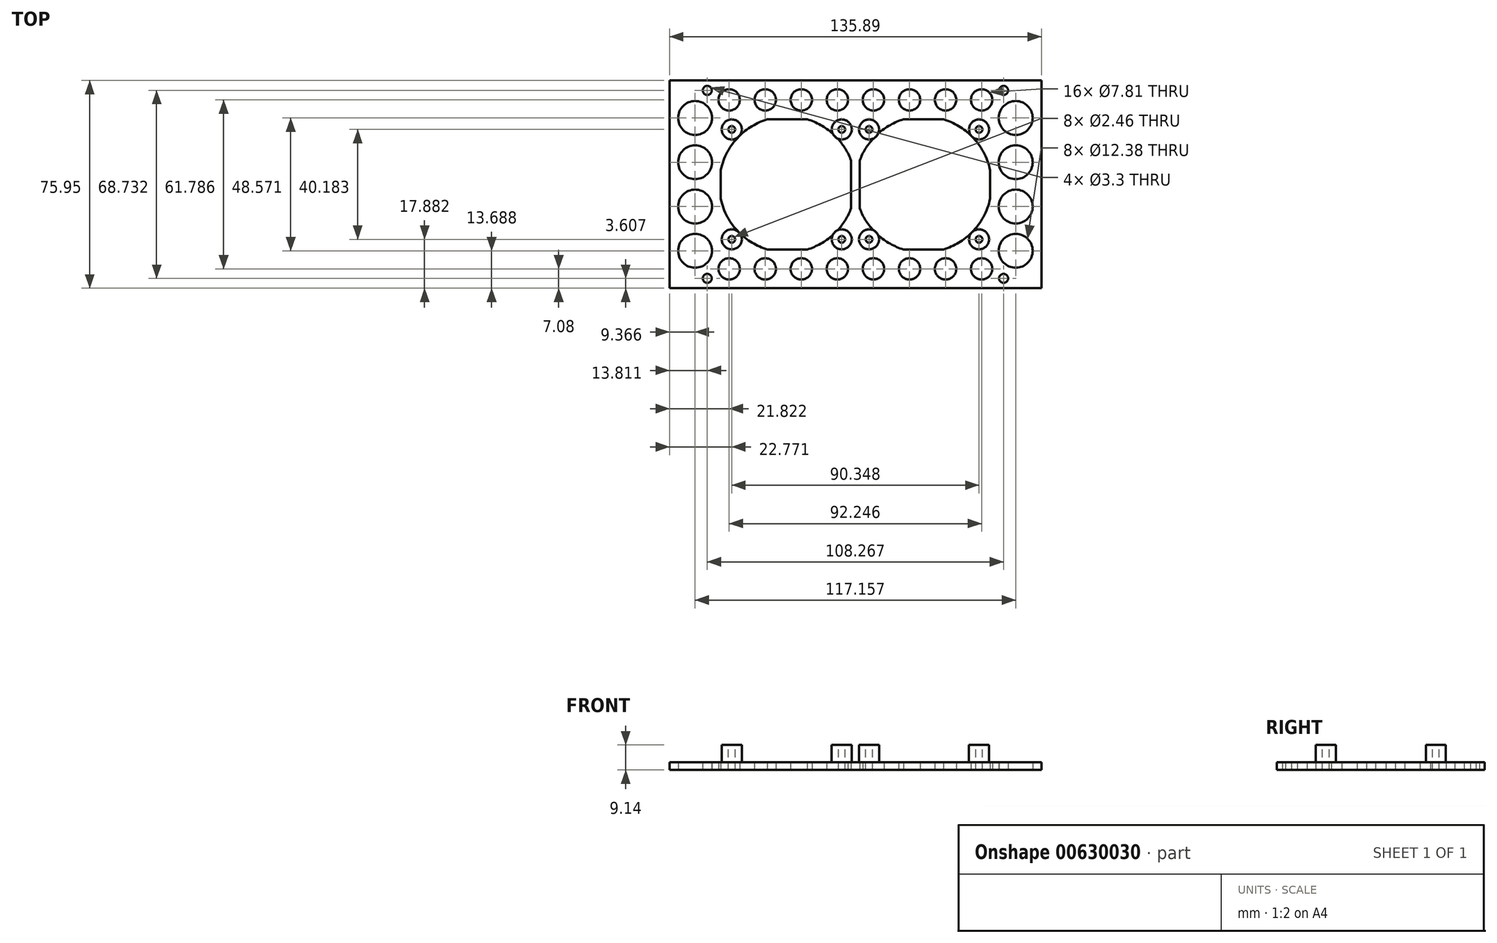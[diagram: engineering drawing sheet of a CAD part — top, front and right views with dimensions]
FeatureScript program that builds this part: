
annotation { "Feature Type Name" : "Feature", "Feature Type Description" : "" }
export const myFeature = defineFeature(function(context is Context, id is Id, definition is map)
    precondition{}
    {
        {
            var Q0;
            Q0=qCreatedBy(makeId("Top.planeOp"),FACE);
            var sketch = newSketch(context, id + "F0", { "sketchPlane" : qUnion([Q0])});
            skLineSegment(sketch, "E0.bottom", {"start": v(0, 0) * mm, "end": v(135.9, 0) * mm});
            skLineSegment(sketch, "E0.top", {"start": v(0, 75.95) * mm, "end": v(135.9, 75.95) * mm});
            skLineSegment(sketch, "E0.left", {"start": v(0, 0) * mm, "end": v(0, 75.95) * mm});
            skLineSegment(sketch, "E0.right", {"start": v(135.9, 0) * mm, "end": v(135.9, 75.95) * mm});
            skLineSegment(sketch, "E1", {"start": v(67.95, 0) * mm, "end": v(67.95, 37.97) * mm, "construction": true});
            skLineSegment(sketch, "E2", {"start": v(0, 37.97) * mm, "end": v(176.32, 37.97) * mm, "construction": true});
            skCircle(sketch, "E3", {"center": v(13.81, 72.34) * mm, "radius": 1.65 * mm});
            skCircle(sketch, "E4.MirrorC", {"center": v(122.08, 72.34) * mm, "radius": 1.65 * mm});
            skCircle(sketch, "E5.MirrorC", {"center": v(13.81, 3.6) * mm, "radius": 1.65 * mm});
            skCircle(sketch, "E6.MirrorC", {"center": v(122.08, 3.6) * mm, "radius": 1.65 * mm});
            skLineSegment(sketch, "E7.bottom", {"start": v(35.8, 61.79) * mm, "end": v(50.3, 61.79) * mm});
            skLineSegment(sketch, "E7.top", {"start": v(35.8, 14.16) * mm, "end": v(50.3, 14.16) * mm});
            skLineSegment(sketch, "E7.left", {"start": v(18.73, 43.28) * mm, "end": v(18.73, 32.67) * mm});
            skLineSegment(sketch, "E7.right", {"start": v(117.16, 43.28) * mm, "end": v(117.16, 32.67) * mm});
            skLineSegment(sketch, "E8", {"start": v(18.73, 61.79) * mm, "end": v(117.16, 14.16) * mm, "construction": true});
            skArc(sketch, "E9", {"start": v(66.36, 46.72) * mm, "mid": v(60.09, 56.12) * mm, "end": v(50.3, 61.79) * mm});
            skArc(sketch, "E10.MirrorC", {"start": v(69.53, 46.72) * mm, "mid": v(75.8, 56.12) * mm, "end": v(85.59, 61.79) * mm});
            skLineSegment(sketch, "E11", {"start": v(66.36, 29.23) * mm, "end": v(66.36, 46.72) * mm});
            skLineSegment(sketch, "E12.MirrorCS", {"start": v(69.53, 29.23) * mm, "end": v(69.53, 46.72) * mm});
            skPoint(sketch, "E13.orphan", {"position": v(66.36, 52.96) * mm});
            skPoint(sketch, "E14.orphan", {"position": v(69.53, 52.96) * mm});
            skPoint(sketch, "E15.orphan", {"position": v(66.36, 20.8) * mm});
            skPoint(sketch, "E16.orphan", {"position": v(69.53, 20.8) * mm});
            skLineSegment(sketch, "E17.trimOffspring", {"start": v(85.59, 14.16) * mm, "end": v(100.09, 14.16) * mm});
            skLineSegment(sketch, "E18.trimOffspring", {"start": v(85.59, 61.79) * mm, "end": v(100.09, 61.79) * mm});
            skArc(sketch, "E19.trimOffspring", {"start": v(85.59, 14.16) * mm, "mid": v(75.8, 19.82) * mm, "end": v(69.53, 29.23) * mm});
            skArc(sketch, "E20.trimOffspring", {"start": v(117.16, 32.67) * mm, "mid": v(111.14, 21.1) * mm, "end": v(100.09, 14.16) * mm});
            skArc(sketch, "E21.trimOffspring", {"start": v(100.09, 61.79) * mm, "mid": v(111.14, 54.85) * mm, "end": v(117.16, 43.28) * mm});
            skArc(sketch, "E22.trimOffspring", {"start": v(35.8, 61.79) * mm, "mid": v(24.75, 54.85) * mm, "end": v(18.73, 43.28) * mm});
            skArc(sketch, "E23.trimOffspring", {"start": v(18.73, 32.67) * mm, "mid": v(24.75, 21.1) * mm, "end": v(35.8, 14.16) * mm});
            skArc(sketch, "E24.trimOffspring", {"start": v(50.3, 14.16) * mm, "mid": v(60.09, 19.82) * mm, "end": v(66.36, 29.23) * mm});
            skSolve(sketch);
        }
        {
            var Q0;
            Q0 = qSketchRegion(id + "F0", true);
            extrude(context, id + "F1", {"entities" : qUnion([Q0]), "depth" : 2.8 * mm, "offsetDistance" : 25.4 * mm});
        }
        {
            var Q0;
            Q0=makeQuery(id+"F1.opExtrude","CAP_FACE",FACE,{"disambiguationData":[OSD([sQuery(id+"F0.wireOp",EDGE,"E0.bottom"),sQuery(id+"F0.wireOp",EDGE,"E0.top"),sQuery(id+"F0.wireOp",EDGE,"E0.left"),sQuery(id+"F0.wireOp",EDGE,"E0.right"),sQuery(id+"F0.wireOp",EDGE,"E3"),sQuery(id+"F0.wireOp",EDGE,"E4.MirrorC"),sQuery(id+"F0.wireOp",EDGE,"E5.MirrorC"),sQuery(id+"F0.wireOp",EDGE,"E6.MirrorC"),sQuery(id+"F0.wireOp",EDGE,"E7.bottom"),sQuery(id+"F0.wireOp",EDGE,"E7.top"),sQuery(id+"F0.wireOp",EDGE,"E7.left"),sQuery(id+"F0.wireOp",EDGE,"E7.right"),sQuery(id+"F0.wireOp",EDGE,"E9"),sQuery(id+"F0.wireOp",EDGE,"E10.MirrorC"),sQuery(id+"F0.wireOp",EDGE,"E11"),sQuery(id+"F0.wireOp",EDGE,"E12.MirrorCS"),sQuery(id+"F0.wireOp",EDGE,"E17.trimOffspring"),sQuery(id+"F0.wireOp",EDGE,"E18.trimOffspring"),sQuery(id+"F0.wireOp",EDGE,"E19.trimOffspring"),sQuery(id+"F0.wireOp",EDGE,"E20.trimOffspring"),sQuery(id+"F0.wireOp",EDGE,"E21.trimOffspring"),sQuery(id+"F0.wireOp",EDGE,"E22.trimOffspring"),sQuery(id+"F0.wireOp",EDGE,"E23.trimOffspring"),sQuery(id+"F0.wireOp",EDGE,"E24.trimOffspring")])],"isStart":false});
            var sketch = newSketch(context, id + "F2", { "sketchPlane" : qUnion([Q0])});
            skSolve(sketch);
        }
        {
            var Q0;
            Q0=makeQuery(id+"F2.imprint","IMPRINT",FACE,{"disambiguationData":[TD([[makeQuery(id+"F2.imprint","IMPRINT",EDGE,{"derivedFrom":makeQuery(id+"F1.opExtrude","CAP_EDGE",EDGE,{"disambiguationData":[OSD([sQuery(id+"F0.wireOp",EDGE,"E0.bottom")])],"isStart":false})}),1.0]])]});
            var sketch = newSketch(context, id + "F3", { "sketchPlane" : qUnion([Q0])});
            skLineSegment(sketch, "E25", {"start": v(66.36, 37.97) * mm, "end": v(69.53, 37.97) * mm, "construction": true});
            skLineSegment(sketch, "E26", {"start": v(67.94, 78.79) * mm, "end": v(67.94, 37.97) * mm, "construction": true});
            skCircle(sketch, "E27", {"center": v(22.77, 58.06) * mm, "radius": 1.23 * mm});
            skCircle(sketch, "E28", {"center": v(62.95, 58.06) * mm, "radius": 1.23 * mm});
            skCircle(sketch, "E29.MirrorC", {"center": v(72.94, 58.06) * mm, "radius": 1.23 * mm});
            skCircle(sketch, "E30.MirrorC", {"center": v(113.12, 58.06) * mm, "radius": 1.23 * mm});
            skCircle(sketch, "E31.MirrorC", {"center": v(113.12, 17.88) * mm, "radius": 1.23 * mm});
            skCircle(sketch, "E32.MirrorC", {"center": v(72.94, 17.88) * mm, "radius": 1.23 * mm});
            skCircle(sketch, "E33.MirrorC", {"center": v(62.95, 17.88) * mm, "radius": 1.23 * mm});
            skCircle(sketch, "E34.MirrorC", {"center": v(22.77, 17.88) * mm, "radius": 1.23 * mm});
            skSolve(sketch);
        }
        {
            var Q0;
            Q0 = qSketchRegion(id + "F3", true);
            extrude(context, id + "F4", {"entities" : qUnion([Q0]), "operationType" : NewBodyOperationType.REMOVE, "endBound" : BoundingType.THROUGH_ALL, "oppositeDirection" : true, "depth" : 25.4 * mm, "offsetDistance" : 25.4 * mm});
        }
        {
            var Q0;
            Q0=makeQuery(id+"F2.imprint","IMPRINT",FACE,{"disambiguationData":[TD([[makeQuery(id+"F2.imprint","IMPRINT",EDGE,{"derivedFrom":makeQuery(id+"F1.opExtrude","CAP_EDGE",EDGE,{"disambiguationData":[OSD([sQuery(id+"F0.wireOp",EDGE,"E0.bottom")])],"isStart":false})}),1.0]])]});
            var sketch = newSketch(context, id + "F5", { "sketchPlane" : qUnion([Q0])});
            skCircle(sketch, "E35.0", {"center": v(22.77, 58.06) * mm, "radius": 1.23 * mm});
            skCircle(sketch, "E35.1", {"center": v(22.77, 17.88) * mm, "radius": 1.23 * mm});
            skCircle(sketch, "E35.2", {"center": v(62.95, 17.88) * mm, "radius": 1.23 * mm});
            skCircle(sketch, "E35.3", {"center": v(62.95, 58.06) * mm, "radius": 1.23 * mm});
            skCircle(sketch, "E35.4", {"center": v(72.94, 58.06) * mm, "radius": 1.23 * mm});
            skCircle(sketch, "E35.5", {"center": v(72.94, 17.88) * mm, "radius": 1.23 * mm});
            skCircle(sketch, "E35.6", {"center": v(113.12, 58.06) * mm, "radius": 1.23 * mm});
            skCircle(sketch, "E35.7", {"center": v(113.12, 17.88) * mm, "radius": 1.23 * mm});
            skCircle(sketch, "E36", {"center": v(22.77, 58.06) * mm, "radius": 3.66 * mm});
            skCircle(sketch, "E37", {"center": v(62.95, 58.06) * mm, "radius": 3.66 * mm});
            skCircle(sketch, "E38", {"center": v(72.94, 58.06) * mm, "radius": 3.66 * mm});
            skCircle(sketch, "E39", {"center": v(113.12, 58.06) * mm, "radius": 3.66 * mm});
            skCircle(sketch, "E40", {"center": v(113.12, 17.88) * mm, "radius": 3.66 * mm});
            skCircle(sketch, "E41", {"center": v(72.94, 17.88) * mm, "radius": 3.66 * mm});
            skCircle(sketch, "E42", {"center": v(62.95, 17.88) * mm, "radius": 3.66 * mm});
            skCircle(sketch, "E43", {"center": v(22.77, 17.88) * mm, "radius": 3.66 * mm});
            skSolve(sketch);
        }
        {
            var Q0;
            Q0 = qSketchRegion(id + "F5", true);
            extrude(context, id + "F6", {"entities" : qUnion([Q0]), "operationType" : NewBodyOperationType.ADD, "depth" : 6.35 * mm, "offsetDistance" : 25.4 * mm});
        }
        {
            var Q0;
            Q0=makeQuery(id+"F1.opExtrude","CAP_FACE",FACE,{"disambiguationData":[OSD([sQuery(id+"F0.wireOp",EDGE,"E0.bottom"),sQuery(id+"F0.wireOp",EDGE,"E0.top"),sQuery(id+"F0.wireOp",EDGE,"E0.left"),sQuery(id+"F0.wireOp",EDGE,"E0.right"),sQuery(id+"F0.wireOp",EDGE,"E3"),sQuery(id+"F0.wireOp",EDGE,"E4.MirrorC"),sQuery(id+"F0.wireOp",EDGE,"E5.MirrorC"),sQuery(id+"F0.wireOp",EDGE,"E6.MirrorC"),sQuery(id+"F0.wireOp",EDGE,"E7.bottom"),sQuery(id+"F0.wireOp",EDGE,"E7.top"),sQuery(id+"F0.wireOp",EDGE,"E7.left"),sQuery(id+"F0.wireOp",EDGE,"E7.right"),sQuery(id+"F0.wireOp",EDGE,"E9"),sQuery(id+"F0.wireOp",EDGE,"E10.MirrorC"),sQuery(id+"F0.wireOp",EDGE,"E11"),sQuery(id+"F0.wireOp",EDGE,"E12.MirrorCS"),sQuery(id+"F0.wireOp",EDGE,"E17.trimOffspring"),sQuery(id+"F0.wireOp",EDGE,"E18.trimOffspring"),sQuery(id+"F0.wireOp",EDGE,"E19.trimOffspring"),sQuery(id+"F0.wireOp",EDGE,"E20.trimOffspring"),sQuery(id+"F0.wireOp",EDGE,"E21.trimOffspring"),sQuery(id+"F0.wireOp",EDGE,"E22.trimOffspring"),sQuery(id+"F0.wireOp",EDGE,"E23.trimOffspring"),sQuery(id+"F0.wireOp",EDGE,"E24.trimOffspring")])],"isStart":true});
            var sketch = newSketch(context, id + "F7", { "sketchPlane" : qUnion([Q0])});
            skLineSegment(sketch, "E44.bottom", {"start": v(15.56, -10.99) * mm, "end": v(120.33, -10.99) * mm, "construction": true});
            skLineSegment(sketch, "E44.top", {"start": v(15.56, -64.96) * mm, "end": v(120.33, -64.96) * mm, "construction": true});
            skLineSegment(sketch, "E44.left", {"start": v(15.56, -10.99) * mm, "end": v(15.56, -64.96) * mm, "construction": true});
            skLineSegment(sketch, "E44.right", {"start": v(120.33, -10.99) * mm, "end": v(120.33, -64.96) * mm, "construction": true});
            skLineSegment(sketch, "E45.0", {"start": v(3.17, -72.77) * mm, "end": v(9, -72.77) * mm, "construction": true});
            skLineSegment(sketch, "E45.1", {"start": v(3.17, -3.17) * mm, "end": v(3.17, -72.77) * mm, "construction": true});
            skLineSegment(sketch, "E45.2", {"start": v(3.17, -3.17) * mm, "end": v(9, -3.17) * mm, "construction": true});
            skLineSegment(sketch, "E45.3", {"start": v(132.72, -3.17) * mm, "end": v(132.72, -72.77) * mm, "construction": true});
            skArc(sketch, "E46.0", {"start": v(18.62, -72.77) * mm, "mid": v(13.81, -67.51) * mm, "end": v(9, -72.77) * mm, "construction": true});
            skLineSegment(sketch, "E47", {"start": v(67.95, -75.95) * mm, "end": v(67.95, -37.97) * mm, "construction": true});
            skLineSegment(sketch, "E48", {"start": v(67.95, -37.97) * mm, "end": v(0, -37.97) * mm, "construction": true});
            skArc(sketch, "E49.MirrorC", {"start": v(117.27, -72.77) * mm, "mid": v(122.08, -67.51) * mm, "end": v(126.89, -72.77) * mm, "construction": true});
            skArc(sketch, "E50.MirrorC", {"start": v(18.62, -3.17) * mm, "mid": v(13.81, -8.43) * mm, "end": v(9, -3.17) * mm, "construction": true});
            skArc(sketch, "E51.MirrorC", {"start": v(117.27, -3.17) * mm, "mid": v(122.08, -8.43) * mm, "end": v(126.89, -3.18) * mm, "construction": true});
            skLineSegment(sketch, "E52.trimOffspring", {"start": v(18.62, -72.77) * mm, "end": v(117.27, -72.77) * mm, "construction": true});
            skLineSegment(sketch, "E53.trimOffspring", {"start": v(126.89, -72.77) * mm, "end": v(132.72, -72.77) * mm, "construction": true});
            skLineSegment(sketch, "E54.trimOffspring", {"start": v(126.89, -3.17) * mm, "end": v(132.72, -3.17) * mm, "construction": true});
            skLineSegment(sketch, "E55.trimOffspring", {"start": v(18.62, -3.17) * mm, "end": v(117.27, -3.17) * mm, "construction": true});
            skCircle(sketch, "E56", {"center": v(9.37, -62.26) * mm, "radius": 6.2 * mm});
            skCircle(sketch, "E57", {"center": v(9.37, -46.07) * mm, "radius": 6.2 * mm});
            skCircle(sketch, "E58", {"center": v(21.82, -68.87) * mm, "radius": 3.9 * mm});
            skCircle(sketch, "E59", {"center": v(35, -68.87) * mm, "radius": 3.9 * mm});
            skCircle(sketch, "E60", {"center": v(48.18, -68.87) * mm, "radius": 3.9 * mm});
            skCircle(sketch, "E61", {"center": v(61.36, -68.87) * mm, "radius": 3.9 * mm});
            skLineSegment(sketch, "E62", {"start": v(9.37, -62.26) * mm, "end": v(9.37, -46.07) * mm, "construction": true});
            skLineSegment(sketch, "E63", {"start": v(9.37, -46.07) * mm, "end": v(9.37, -29.88) * mm, "construction": true});
            skLineSegment(sketch, "E64", {"start": v(21.82, -68.87) * mm, "end": v(35, -68.87) * mm, "construction": true});
            skLineSegment(sketch, "E65", {"start": v(48.18, -68.87) * mm, "end": v(35, -68.87) * mm, "construction": true});
            skLineSegment(sketch, "E66", {"start": v(48.18, -68.87) * mm, "end": v(61.36, -68.87) * mm, "construction": true});
            skLineSegment(sketch, "E67", {"start": v(61.36, -68.87) * mm, "end": v(74.53, -68.87) * mm, "construction": true});
            skCircle(sketch, "E68.MirrorC", {"center": v(126.52, -46.07) * mm, "radius": 6.2 * mm});
            skCircle(sketch, "E69.MirrorC", {"center": v(126.52, -62.26) * mm, "radius": 6.2 * mm});
            skCircle(sketch, "E70.MirrorC", {"center": v(74.53, -68.87) * mm, "radius": 3.9 * mm});
            skCircle(sketch, "E71.MirrorC", {"center": v(87.71, -68.87) * mm, "radius": 3.9 * mm});
            skCircle(sketch, "E72.MirrorC", {"center": v(100.9, -68.87) * mm, "radius": 3.9 * mm});
            skCircle(sketch, "E73.MirrorC", {"center": v(114.07, -68.87) * mm, "radius": 3.9 * mm});
            skCircle(sketch, "E74.MirrorC", {"center": v(126.52, -29.88) * mm, "radius": 6.2 * mm});
            skCircle(sketch, "E75.MirrorC", {"center": v(126.52, -13.69) * mm, "radius": 6.2 * mm});
            skCircle(sketch, "E76.MirrorC", {"center": v(114.07, -7.08) * mm, "radius": 3.9 * mm});
            skCircle(sketch, "E77.MirrorC", {"center": v(100.9, -7.08) * mm, "radius": 3.9 * mm});
            skCircle(sketch, "E78.MirrorC", {"center": v(87.71, -7.08) * mm, "radius": 3.9 * mm});
            skCircle(sketch, "E79.MirrorC", {"center": v(74.53, -7.08) * mm, "radius": 3.9 * mm});
            skCircle(sketch, "E80.MirrorC", {"center": v(61.36, -7.08) * mm, "radius": 3.9 * mm});
            skCircle(sketch, "E81.MirrorC", {"center": v(48.18, -7.08) * mm, "radius": 3.9 * mm});
            skCircle(sketch, "E82.MirrorC", {"center": v(35, -7.08) * mm, "radius": 3.9 * mm});
            skCircle(sketch, "E83.MirrorC", {"center": v(21.82, -7.08) * mm, "radius": 3.9 * mm});
            skCircle(sketch, "E84.MirrorC", {"center": v(9.37, -13.69) * mm, "radius": 6.2 * mm});
            skCircle(sketch, "E85.MirrorC", {"center": v(9.37, -29.88) * mm, "radius": 6.2 * mm});
            skSolve(sketch);
        }
        {
            var Q0;
            Q0 = qSketchRegion(id + "F7", true);
            extrude(context, id + "F8", {"entities" : qUnion([Q0]), "operationType" : NewBodyOperationType.REMOVE, "endBound" : BoundingType.THROUGH_ALL, "oppositeDirection" : true, "depth" : 25.4 * mm, "offsetDistance" : 25.4 * mm});
        }
    });
